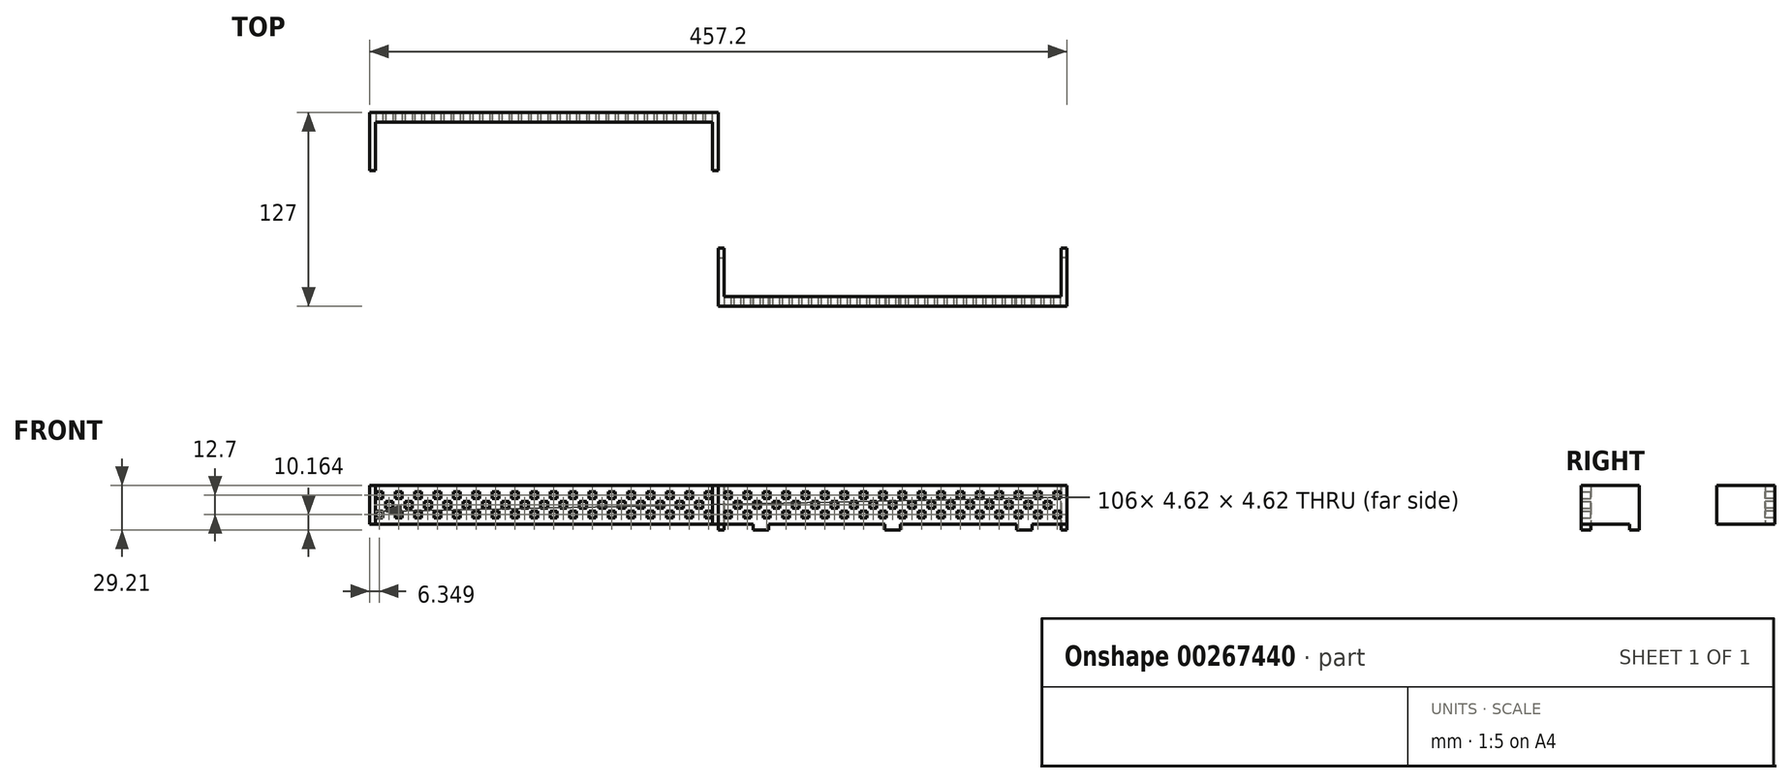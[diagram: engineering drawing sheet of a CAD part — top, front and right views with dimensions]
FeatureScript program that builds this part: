
annotation { "Feature Type Name" : "Feature", "Feature Type Description" : "" }
export const myFeature = defineFeature(function(context is Context, id is Id, definition is map)
    precondition{}
    {
        {
            var Q0;
            Q0=qCreatedBy(makeId("Front.planeOp"),FACE);
            var sketch = newSketch(context, id + "F0", { "sketchPlane" : qUnion([Q0])});
            skLineSegment(sketch, "E0", {"start": v(-96.7, -7.19) * mm, "end": v(-84, -7.19) * mm});
            skLineSegment(sketch, "E1.1.0.0", {"start": v(-84, -7.19) * mm, "end": v(-71.3, -7.19) * mm});
            skLineSegment(sketch, "E1.2.0.0", {"start": v(-71.3, -7.19) * mm, "end": v(-58.6, -7.19) * mm});
            skLineSegment(sketch, "E1.3.0.0", {"start": v(-58.6, -7.19) * mm, "end": v(-45.9, -7.19) * mm});
            skLineSegment(sketch, "E1.4.0.0", {"start": v(-45.9, -7.19) * mm, "end": v(-33.2, -7.19) * mm});
            skLineSegment(sketch, "E1.5.0.0", {"start": v(-33.2, -7.19) * mm, "end": v(-20.5, -7.19) * mm});
            skLineSegment(sketch, "E1.6.0.0", {"start": v(-20.5, -7.19) * mm, "end": v(-7.8, -7.19) * mm});
            skLineSegment(sketch, "E1.7.0.0", {"start": v(-7.8, -7.19) * mm, "end": v(4.9, -7.19) * mm});
            skLineSegment(sketch, "E1.8.0.0", {"start": v(4.9, -7.19) * mm, "end": v(17.6, -7.19) * mm});
            skLineSegment(sketch, "E1.9.0.0", {"start": v(17.6, -7.19) * mm, "end": v(30.3, -7.19) * mm});
            skLineSegment(sketch, "E1.10.0.0", {"start": v(30.3, -7.19) * mm, "end": v(43, -7.19) * mm});
            skLineSegment(sketch, "E1.11.0.0", {"start": v(43, -7.19) * mm, "end": v(55.7, -7.19) * mm});
            skLineSegment(sketch, "E1.12.0.0", {"start": v(55.7, -7.19) * mm, "end": v(68.4, -7.19) * mm});
            skLineSegment(sketch, "E1.13.0.0", {"start": v(68.4, -7.19) * mm, "end": v(81.1, -7.19) * mm});
            skLineSegment(sketch, "E1.14.0.0", {"start": v(81.1, -7.19) * mm, "end": v(93.8, -7.19) * mm});
            skLineSegment(sketch, "E1.direction1", {"start": v(-96.7, -7.19) * mm, "end": v(-84, -7.19) * mm, "construction": true});
            skLineSegment(sketch, "E2", {"start": v(-96.7, -7.19) * mm, "end": v(-96.7, 5.51) * mm});
            skLineSegment(sketch, "E3", {"start": v(-96.7, -0.84) * mm, "end": v(-84.12, -0.84) * mm});
            skPoint(sketch, "E3.endSnap0", {"position": v(-96.7, -0.84) * mm});
            skLineSegment(sketch, "E4.MirrorCS", {"start": v(-96.7, 5.51) * mm, "end": v(-84, 5.51) * mm, "construction": true});
            skLineSegment(sketch, "E5.MirrorCS", {"start": v(-84, 5.51) * mm, "end": v(-71.3, 5.51) * mm});
            skLineSegment(sketch, "E6.MirrorCS", {"start": v(-71.3, 5.51) * mm, "end": v(-58.6, 5.51) * mm});
            skLineSegment(sketch, "E7.MirrorCS", {"start": v(-58.6, 5.51) * mm, "end": v(-45.9, 5.51) * mm});
            skLineSegment(sketch, "E8.MirrorCS", {"start": v(-45.9, 5.51) * mm, "end": v(-33.2, 5.51) * mm});
            skLineSegment(sketch, "E9.MirrorCS", {"start": v(-33.2, 5.51) * mm, "end": v(-20.5, 5.51) * mm});
            skLineSegment(sketch, "E10.MirrorCS", {"start": v(-20.5, 5.51) * mm, "end": v(-7.8, 5.51) * mm});
            skLineSegment(sketch, "E11.MirrorCS", {"start": v(-7.8, 5.51) * mm, "end": v(-5.49, 5.51) * mm});
            skLineSegment(sketch, "E12.MirrorCS", {"start": v(4.9, 5.51) * mm, "end": v(7.21, 5.51) * mm});
            skLineSegment(sketch, "E13.MirrorCS", {"start": v(17.6, 5.51) * mm, "end": v(19.91, 5.51) * mm});
            skLineSegment(sketch, "E14.MirrorCS", {"start": v(55.7, 5.51) * mm, "end": v(68.4, 5.51) * mm});
            skLineSegment(sketch, "E15.MirrorCS", {"start": v(55.7, 5.51) * mm, "end": v(58.01, 5.51) * mm});
            skLineSegment(sketch, "E16.MirrorCS", {"start": v(30.3, 5.51) * mm, "end": v(32.61, 5.51) * mm});
            skLineSegment(sketch, "E17.MirrorCS", {"start": v(68.4, 5.51) * mm, "end": v(81.1, 5.51) * mm});
            skLineSegment(sketch, "E18.MirrorCS", {"start": v(81.1, 5.51) * mm, "end": v(93.8, 5.51) * mm});
            skLineSegment(sketch, "E19.MirrorCS", {"start": v(43, 5.51) * mm, "end": v(45.31, 5.51) * mm});
            skLineSegment(sketch, "E20.bottom", {"start": v(-99.01, -9.5) * mm, "end": v(-94.39, -9.5) * mm});
            skLineSegment(sketch, "E20.top", {"start": v(-99.01, -4.87) * mm, "end": v(-94.39, -4.87) * mm});
            skLineSegment(sketch, "E20.left", {"start": v(-99.01, -9.5) * mm, "end": v(-99.01, -4.87) * mm});
            skLineSegment(sketch, "E20.right", {"start": v(-94.39, -9.5) * mm, "end": v(-94.39, -4.87) * mm});
            skPoint(sketch, "E20.middle", {"position": v(-96.7, -7.19) * mm});
            skLineSegment(sketch, "E21.0.1.0", {"start": v(-94.39, 3.2) * mm, "end": v(-94.39, 7.83) * mm});
            skLineSegment(sketch, "E21.0.1.1", {"start": v(-99.01, 3.2) * mm, "end": v(-99.01, 7.83) * mm});
            skLineSegment(sketch, "E21.0.1.2", {"start": v(-99.01, 7.83) * mm, "end": v(-94.39, 7.83) * mm});
            skLineSegment(sketch, "E21.0.1.3", {"start": v(-99.01, 3.2) * mm, "end": v(-94.39, 3.2) * mm});
            skLineSegment(sketch, "E21.1.0.0", {"start": v(-81.69, -9.5) * mm, "end": v(-81.69, -4.87) * mm});
            skLineSegment(sketch, "E21.1.0.1", {"start": v(-86.31, -9.5) * mm, "end": v(-86.31, -4.87) * mm});
            skLineSegment(sketch, "E21.1.0.2", {"start": v(-86.31, -4.87) * mm, "end": v(-81.69, -4.87) * mm});
            skLineSegment(sketch, "E21.1.0.3", {"start": v(-86.31, -9.5) * mm, "end": v(-81.69, -9.5) * mm});
            skLineSegment(sketch, "E21.1.1.0", {"start": v(-81.69, 3.2) * mm, "end": v(-81.69, 7.83) * mm});
            skLineSegment(sketch, "E21.1.1.1", {"start": v(-86.31, 3.2) * mm, "end": v(-86.31, 7.83) * mm});
            skLineSegment(sketch, "E21.1.1.2", {"start": v(-86.31, 7.83) * mm, "end": v(-81.69, 7.83) * mm});
            skLineSegment(sketch, "E21.1.1.3", {"start": v(-86.31, 3.2) * mm, "end": v(-81.69, 3.2) * mm});
            skLineSegment(sketch, "E21.2.0.0", {"start": v(-68.99, -9.5) * mm, "end": v(-68.99, -4.87) * mm});
            skLineSegment(sketch, "E21.2.0.1", {"start": v(-73.61, -9.5) * mm, "end": v(-73.61, -4.87) * mm});
            skLineSegment(sketch, "E21.2.0.2", {"start": v(-73.61, -4.87) * mm, "end": v(-68.99, -4.87) * mm});
            skLineSegment(sketch, "E21.2.0.3", {"start": v(-73.61, -9.5) * mm, "end": v(-68.99, -9.5) * mm});
            skLineSegment(sketch, "E21.2.1.0", {"start": v(-68.99, 3.2) * mm, "end": v(-68.99, 7.83) * mm});
            skLineSegment(sketch, "E21.2.1.1", {"start": v(-73.61, 3.2) * mm, "end": v(-73.61, 7.83) * mm});
            skLineSegment(sketch, "E21.2.1.2", {"start": v(-73.61, 7.83) * mm, "end": v(-68.99, 7.83) * mm});
            skLineSegment(sketch, "E21.2.1.3", {"start": v(-73.61, 3.2) * mm, "end": v(-68.99, 3.2) * mm});
            skLineSegment(sketch, "E21.3.0.0", {"start": v(-56.29, -9.5) * mm, "end": v(-56.29, -4.87) * mm});
            skLineSegment(sketch, "E21.3.0.1", {"start": v(-60.91, -9.5) * mm, "end": v(-60.91, -4.87) * mm});
            skLineSegment(sketch, "E21.3.0.2", {"start": v(-60.91, -4.87) * mm, "end": v(-56.29, -4.87) * mm});
            skLineSegment(sketch, "E21.3.0.3", {"start": v(-60.91, -9.5) * mm, "end": v(-56.29, -9.5) * mm});
            skLineSegment(sketch, "E21.3.1.0", {"start": v(-56.29, 3.2) * mm, "end": v(-56.29, 7.83) * mm});
            skLineSegment(sketch, "E21.3.1.1", {"start": v(-60.91, 3.2) * mm, "end": v(-60.91, 7.83) * mm});
            skLineSegment(sketch, "E21.3.1.2", {"start": v(-60.91, 7.83) * mm, "end": v(-56.29, 7.83) * mm});
            skLineSegment(sketch, "E21.3.1.3", {"start": v(-60.91, 3.2) * mm, "end": v(-56.29, 3.2) * mm});
            skLineSegment(sketch, "E21.4.0.0", {"start": v(-43.59, -9.5) * mm, "end": v(-43.59, -4.87) * mm});
            skLineSegment(sketch, "E21.4.0.1", {"start": v(-48.21, -9.5) * mm, "end": v(-48.21, -4.87) * mm});
            skLineSegment(sketch, "E21.4.0.2", {"start": v(-48.21, -4.87) * mm, "end": v(-43.59, -4.87) * mm});
            skLineSegment(sketch, "E21.4.0.3", {"start": v(-48.21, -9.5) * mm, "end": v(-43.59, -9.5) * mm});
            skLineSegment(sketch, "E21.4.1.0", {"start": v(-43.59, 3.2) * mm, "end": v(-43.59, 7.83) * mm});
            skLineSegment(sketch, "E21.4.1.1", {"start": v(-48.21, 3.2) * mm, "end": v(-48.21, 7.83) * mm});
            skLineSegment(sketch, "E21.4.1.2", {"start": v(-48.21, 7.83) * mm, "end": v(-43.59, 7.83) * mm});
            skLineSegment(sketch, "E21.4.1.3", {"start": v(-48.21, 3.2) * mm, "end": v(-43.59, 3.2) * mm});
            skLineSegment(sketch, "E21.5.0.0", {"start": v(-30.89, -9.5) * mm, "end": v(-30.89, -4.87) * mm});
            skLineSegment(sketch, "E21.5.0.1", {"start": v(-35.51, -9.5) * mm, "end": v(-35.51, -4.87) * mm});
            skLineSegment(sketch, "E21.5.0.2", {"start": v(-35.51, -4.87) * mm, "end": v(-30.89, -4.87) * mm});
            skLineSegment(sketch, "E21.5.0.3", {"start": v(-35.51, -9.5) * mm, "end": v(-30.89, -9.5) * mm});
            skLineSegment(sketch, "E21.5.1.0", {"start": v(-30.89, 3.2) * mm, "end": v(-30.89, 7.83) * mm});
            skLineSegment(sketch, "E21.5.1.1", {"start": v(-35.51, 3.2) * mm, "end": v(-35.51, 7.83) * mm});
            skLineSegment(sketch, "E21.5.1.2", {"start": v(-35.51, 7.83) * mm, "end": v(-30.89, 7.83) * mm});
            skLineSegment(sketch, "E21.5.1.3", {"start": v(-35.51, 3.2) * mm, "end": v(-30.89, 3.2) * mm});
            skLineSegment(sketch, "E21.6.0.0", {"start": v(-18.19, -9.5) * mm, "end": v(-18.19, -4.87) * mm});
            skLineSegment(sketch, "E21.6.0.1", {"start": v(-22.81, -9.5) * mm, "end": v(-22.81, -4.87) * mm});
            skLineSegment(sketch, "E21.6.0.2", {"start": v(-22.81, -4.87) * mm, "end": v(-18.19, -4.87) * mm});
            skLineSegment(sketch, "E21.6.0.3", {"start": v(-22.81, -9.5) * mm, "end": v(-18.19, -9.5) * mm});
            skLineSegment(sketch, "E21.6.1.0", {"start": v(-18.19, 3.2) * mm, "end": v(-18.19, 7.83) * mm});
            skLineSegment(sketch, "E21.6.1.1", {"start": v(-22.81, 3.2) * mm, "end": v(-22.81, 7.83) * mm});
            skLineSegment(sketch, "E21.6.1.2", {"start": v(-22.81, 7.83) * mm, "end": v(-18.19, 7.83) * mm});
            skLineSegment(sketch, "E21.6.1.3", {"start": v(-22.81, 3.2) * mm, "end": v(-18.19, 3.2) * mm});
            skLineSegment(sketch, "E21.7.0.0", {"start": v(-5.49, -9.5) * mm, "end": v(-5.49, -4.87) * mm});
            skLineSegment(sketch, "E21.7.0.1", {"start": v(-10.11, -9.5) * mm, "end": v(-10.11, -4.87) * mm});
            skLineSegment(sketch, "E21.7.0.2", {"start": v(-10.11, -4.87) * mm, "end": v(-5.49, -4.87) * mm});
            skLineSegment(sketch, "E21.7.0.3", {"start": v(-10.11, -9.5) * mm, "end": v(-5.49, -9.5) * mm});
            skLineSegment(sketch, "E21.7.1.0", {"start": v(-5.49, 3.2) * mm, "end": v(-5.49, 7.83) * mm});
            skLineSegment(sketch, "E21.7.1.1", {"start": v(-10.11, 3.2) * mm, "end": v(-10.11, 7.83) * mm});
            skLineSegment(sketch, "E21.7.1.2", {"start": v(-10.11, 7.83) * mm, "end": v(-5.49, 7.83) * mm});
            skLineSegment(sketch, "E21.7.1.3", {"start": v(-10.11, 3.2) * mm, "end": v(-5.49, 3.2) * mm});
            skLineSegment(sketch, "E21.8.0.0", {"start": v(7.21, -9.5) * mm, "end": v(7.21, -4.87) * mm});
            skLineSegment(sketch, "E21.8.0.1", {"start": v(2.59, -9.5) * mm, "end": v(2.59, -4.87) * mm});
            skLineSegment(sketch, "E21.8.0.2", {"start": v(2.59, -4.87) * mm, "end": v(7.21, -4.87) * mm});
            skLineSegment(sketch, "E21.8.0.3", {"start": v(2.59, -9.5) * mm, "end": v(7.21, -9.5) * mm});
            skLineSegment(sketch, "E21.8.1.0", {"start": v(7.21, 3.2) * mm, "end": v(7.21, 7.83) * mm});
            skLineSegment(sketch, "E21.8.1.1", {"start": v(2.59, 3.2) * mm, "end": v(2.59, 7.83) * mm});
            skLineSegment(sketch, "E21.8.1.2", {"start": v(2.59, 7.83) * mm, "end": v(7.21, 7.83) * mm});
            skLineSegment(sketch, "E21.8.1.3", {"start": v(2.59, 3.2) * mm, "end": v(7.21, 3.2) * mm});
            skLineSegment(sketch, "E21.9.0.0", {"start": v(19.91, -9.5) * mm, "end": v(19.91, -4.87) * mm});
            skLineSegment(sketch, "E21.9.0.1", {"start": v(15.29, -9.5) * mm, "end": v(15.29, -4.87) * mm});
            skLineSegment(sketch, "E21.9.0.2", {"start": v(15.29, -4.87) * mm, "end": v(19.91, -4.87) * mm});
            skLineSegment(sketch, "E21.9.0.3", {"start": v(15.29, -9.5) * mm, "end": v(19.91, -9.5) * mm});
            skLineSegment(sketch, "E21.9.1.0", {"start": v(19.91, 3.2) * mm, "end": v(19.91, 7.83) * mm});
            skLineSegment(sketch, "E21.9.1.1", {"start": v(15.29, 3.2) * mm, "end": v(15.29, 7.83) * mm});
            skLineSegment(sketch, "E21.9.1.2", {"start": v(15.29, 7.83) * mm, "end": v(19.91, 7.83) * mm});
            skLineSegment(sketch, "E21.9.1.3", {"start": v(15.29, 3.2) * mm, "end": v(19.91, 3.2) * mm});
            skLineSegment(sketch, "E21.10.0.0", {"start": v(32.61, -9.5) * mm, "end": v(32.61, -4.87) * mm});
            skLineSegment(sketch, "E21.10.0.1", {"start": v(27.99, -9.5) * mm, "end": v(27.99, -4.87) * mm});
            skLineSegment(sketch, "E21.10.0.2", {"start": v(27.99, -4.87) * mm, "end": v(32.61, -4.87) * mm});
            skLineSegment(sketch, "E21.10.0.3", {"start": v(27.99, -9.5) * mm, "end": v(32.61, -9.5) * mm});
            skLineSegment(sketch, "E21.10.1.0", {"start": v(32.61, 3.2) * mm, "end": v(32.61, 7.83) * mm});
            skLineSegment(sketch, "E21.10.1.1", {"start": v(27.99, 3.2) * mm, "end": v(27.99, 7.83) * mm});
            skLineSegment(sketch, "E21.10.1.2", {"start": v(27.99, 7.83) * mm, "end": v(32.61, 7.83) * mm});
            skLineSegment(sketch, "E21.10.1.3", {"start": v(27.99, 3.2) * mm, "end": v(32.61, 3.2) * mm});
            skLineSegment(sketch, "E21.11.0.0", {"start": v(45.31, -9.5) * mm, "end": v(45.31, -4.87) * mm});
            skLineSegment(sketch, "E21.11.0.1", {"start": v(40.69, -9.5) * mm, "end": v(40.69, -4.87) * mm});
            skLineSegment(sketch, "E21.11.0.2", {"start": v(40.69, -4.87) * mm, "end": v(45.31, -4.87) * mm});
            skLineSegment(sketch, "E21.11.0.3", {"start": v(40.69, -9.5) * mm, "end": v(45.31, -9.5) * mm});
            skLineSegment(sketch, "E21.11.1.0", {"start": v(45.31, 3.2) * mm, "end": v(45.31, 7.83) * mm});
            skLineSegment(sketch, "E21.11.1.1", {"start": v(40.69, 3.2) * mm, "end": v(40.69, 7.83) * mm});
            skLineSegment(sketch, "E21.11.1.2", {"start": v(40.69, 7.83) * mm, "end": v(45.31, 7.83) * mm});
            skLineSegment(sketch, "E21.11.1.3", {"start": v(40.69, 3.2) * mm, "end": v(45.31, 3.2) * mm});
            skLineSegment(sketch, "E21.12.0.0", {"start": v(58.01, -9.5) * mm, "end": v(58.01, -4.87) * mm});
            skLineSegment(sketch, "E21.12.0.1", {"start": v(53.39, -9.5) * mm, "end": v(53.39, -4.87) * mm});
            skLineSegment(sketch, "E21.12.0.2", {"start": v(53.39, -4.87) * mm, "end": v(58.01, -4.87) * mm});
            skLineSegment(sketch, "E21.12.0.3", {"start": v(53.39, -9.5) * mm, "end": v(58.01, -9.5) * mm});
            skLineSegment(sketch, "E21.12.1.0", {"start": v(58.01, 3.2) * mm, "end": v(58.01, 7.83) * mm});
            skLineSegment(sketch, "E21.12.1.1", {"start": v(53.39, 3.2) * mm, "end": v(53.39, 7.83) * mm});
            skLineSegment(sketch, "E21.12.1.2", {"start": v(53.39, 7.83) * mm, "end": v(58.01, 7.83) * mm});
            skLineSegment(sketch, "E21.12.1.3", {"start": v(53.39, 3.2) * mm, "end": v(58.01, 3.2) * mm});
            skLineSegment(sketch, "E21.13.0.0", {"start": v(70.71, -9.5) * mm, "end": v(70.71, -4.87) * mm});
            skLineSegment(sketch, "E21.13.0.1", {"start": v(66.09, -9.5) * mm, "end": v(66.09, -4.87) * mm});
            skLineSegment(sketch, "E21.13.0.2", {"start": v(66.09, -4.87) * mm, "end": v(70.71, -4.87) * mm});
            skLineSegment(sketch, "E21.13.0.3", {"start": v(66.09, -9.5) * mm, "end": v(70.71, -9.5) * mm});
            skLineSegment(sketch, "E21.13.1.0", {"start": v(70.71, 3.2) * mm, "end": v(70.71, 7.83) * mm});
            skLineSegment(sketch, "E21.13.1.1", {"start": v(66.09, 3.2) * mm, "end": v(66.09, 7.83) * mm});
            skLineSegment(sketch, "E21.13.1.2", {"start": v(66.09, 7.83) * mm, "end": v(70.71, 7.83) * mm});
            skLineSegment(sketch, "E21.13.1.3", {"start": v(66.09, 3.2) * mm, "end": v(70.71, 3.2) * mm});
            skLineSegment(sketch, "E21.14.0.0", {"start": v(83.41, -9.5) * mm, "end": v(83.41, -4.87) * mm});
            skLineSegment(sketch, "E21.14.0.1", {"start": v(78.79, -9.5) * mm, "end": v(78.79, -4.87) * mm});
            skLineSegment(sketch, "E21.14.0.2", {"start": v(78.79, -4.87) * mm, "end": v(83.41, -4.87) * mm});
            skLineSegment(sketch, "E21.14.0.3", {"start": v(78.79, -9.5) * mm, "end": v(83.41, -9.5) * mm});
            skLineSegment(sketch, "E21.14.1.0", {"start": v(83.41, 3.2) * mm, "end": v(83.41, 7.83) * mm});
            skLineSegment(sketch, "E21.14.1.1", {"start": v(78.79, 3.2) * mm, "end": v(78.79, 7.83) * mm});
            skLineSegment(sketch, "E21.14.1.2", {"start": v(78.79, 7.83) * mm, "end": v(83.41, 7.83) * mm});
            skLineSegment(sketch, "E21.14.1.3", {"start": v(78.79, 3.2) * mm, "end": v(83.41, 3.2) * mm});
            skLineSegment(sketch, "E21.direction1", {"start": v(-94.39, -9.5) * mm, "end": v(-81.69, -9.5) * mm, "construction": true});
            skLineSegment(sketch, "E21.direction2", {"start": v(-94.39, -9.5) * mm, "end": v(-94.39, 3.2) * mm, "construction": true});
            skLineSegment(sketch, "E22.bottom", {"start": v(-88.1, -3.15) * mm, "end": v(-92.72, -3.15) * mm});
            skLineSegment(sketch, "E22.top", {"start": v(-88.1, 1.48) * mm, "end": v(-92.72, 1.48) * mm});
            skLineSegment(sketch, "E22.left", {"start": v(-88.1, -3.15) * mm, "end": v(-88.1, 1.48) * mm});
            skLineSegment(sketch, "E22.right", {"start": v(-92.72, -3.15) * mm, "end": v(-92.72, 1.48) * mm});
            skPoint(sketch, "E22.middle", {"position": v(-90.41, -0.84) * mm});
            skLineSegment(sketch, "E23.1.0.0", {"start": v(-75.4, -3.15) * mm, "end": v(-75.4, 1.48) * mm});
            skLineSegment(sketch, "E23.1.0.1", {"start": v(-75.4, 1.48) * mm, "end": v(-80.02, 1.48) * mm});
            skLineSegment(sketch, "E23.1.0.2", {"start": v(-80.02, -3.15) * mm, "end": v(-80.02, 1.48) * mm});
            skLineSegment(sketch, "E23.1.0.3", {"start": v(-75.4, -3.15) * mm, "end": v(-80.02, -3.15) * mm});
            skLineSegment(sketch, "E23.2.0.0", {"start": v(-62.7, -3.15) * mm, "end": v(-62.7, 1.48) * mm});
            skLineSegment(sketch, "E23.2.0.1", {"start": v(-62.7, 1.48) * mm, "end": v(-67.32, 1.48) * mm});
            skLineSegment(sketch, "E23.2.0.2", {"start": v(-67.32, -3.15) * mm, "end": v(-67.32, 1.48) * mm});
            skLineSegment(sketch, "E23.2.0.3", {"start": v(-62.7, -3.15) * mm, "end": v(-67.32, -3.15) * mm});
            skLineSegment(sketch, "E23.3.0.0", {"start": v(-50, -3.15) * mm, "end": v(-50, 1.48) * mm});
            skLineSegment(sketch, "E23.3.0.1", {"start": v(-50, 1.48) * mm, "end": v(-54.62, 1.48) * mm});
            skLineSegment(sketch, "E23.3.0.2", {"start": v(-54.62, -3.15) * mm, "end": v(-54.62, 1.48) * mm});
            skLineSegment(sketch, "E23.3.0.3", {"start": v(-50, -3.15) * mm, "end": v(-54.62, -3.15) * mm});
            skLineSegment(sketch, "E23.4.0.0", {"start": v(-37.3, -3.15) * mm, "end": v(-37.3, 1.48) * mm});
            skLineSegment(sketch, "E23.4.0.1", {"start": v(-37.3, 1.48) * mm, "end": v(-41.92, 1.48) * mm});
            skLineSegment(sketch, "E23.4.0.2", {"start": v(-41.92, -3.15) * mm, "end": v(-41.92, 1.48) * mm});
            skLineSegment(sketch, "E23.4.0.3", {"start": v(-37.3, -3.15) * mm, "end": v(-41.92, -3.15) * mm});
            skLineSegment(sketch, "E23.5.0.0", {"start": v(-24.6, -3.15) * mm, "end": v(-24.6, 1.48) * mm});
            skLineSegment(sketch, "E23.5.0.1", {"start": v(-24.6, 1.48) * mm, "end": v(-29.22, 1.48) * mm});
            skLineSegment(sketch, "E23.5.0.2", {"start": v(-29.22, -3.15) * mm, "end": v(-29.22, 1.48) * mm});
            skLineSegment(sketch, "E23.5.0.3", {"start": v(-24.6, -3.15) * mm, "end": v(-29.22, -3.15) * mm});
            skLineSegment(sketch, "E23.6.0.0", {"start": v(-11.9, -3.15) * mm, "end": v(-11.9, 1.48) * mm});
            skLineSegment(sketch, "E23.6.0.1", {"start": v(-11.9, 1.48) * mm, "end": v(-16.52, 1.48) * mm});
            skLineSegment(sketch, "E23.6.0.2", {"start": v(-16.52, -3.15) * mm, "end": v(-16.52, 1.48) * mm});
            skLineSegment(sketch, "E23.6.0.3", {"start": v(-11.9, -3.15) * mm, "end": v(-16.52, -3.15) * mm});
            skLineSegment(sketch, "E23.7.0.0", {"start": v(0.8, -3.15) * mm, "end": v(0.8, 1.48) * mm});
            skLineSegment(sketch, "E23.7.0.1", {"start": v(0.8, 1.48) * mm, "end": v(-3.82, 1.48) * mm});
            skLineSegment(sketch, "E23.7.0.2", {"start": v(-3.82, -3.15) * mm, "end": v(-3.82, 1.48) * mm});
            skLineSegment(sketch, "E23.7.0.3", {"start": v(0.8, -3.15) * mm, "end": v(-3.82, -3.15) * mm});
            skLineSegment(sketch, "E23.8.0.0", {"start": v(13.5, -3.15) * mm, "end": v(13.5, 1.48) * mm});
            skLineSegment(sketch, "E23.8.0.1", {"start": v(13.5, 1.48) * mm, "end": v(8.88, 1.48) * mm});
            skLineSegment(sketch, "E23.8.0.2", {"start": v(8.88, -3.15) * mm, "end": v(8.88, 1.48) * mm});
            skLineSegment(sketch, "E23.8.0.3", {"start": v(13.5, -3.15) * mm, "end": v(8.88, -3.15) * mm});
            skLineSegment(sketch, "E23.9.0.0", {"start": v(26.2, -3.15) * mm, "end": v(26.2, 1.48) * mm});
            skLineSegment(sketch, "E23.9.0.1", {"start": v(26.2, 1.48) * mm, "end": v(21.58, 1.48) * mm});
            skLineSegment(sketch, "E23.9.0.2", {"start": v(21.58, -3.15) * mm, "end": v(21.58, 1.48) * mm});
            skLineSegment(sketch, "E23.9.0.3", {"start": v(26.2, -3.15) * mm, "end": v(21.58, -3.15) * mm});
            skLineSegment(sketch, "E23.10.0.0", {"start": v(38.9, -3.15) * mm, "end": v(38.9, 1.48) * mm});
            skLineSegment(sketch, "E23.10.0.1", {"start": v(38.9, 1.48) * mm, "end": v(34.28, 1.48) * mm});
            skLineSegment(sketch, "E23.10.0.2", {"start": v(34.28, -3.15) * mm, "end": v(34.28, 1.48) * mm});
            skLineSegment(sketch, "E23.10.0.3", {"start": v(38.9, -3.15) * mm, "end": v(34.28, -3.15) * mm});
            skLineSegment(sketch, "E23.11.0.0", {"start": v(51.6, -3.15) * mm, "end": v(51.6, 1.48) * mm});
            skLineSegment(sketch, "E23.11.0.1", {"start": v(51.6, 1.48) * mm, "end": v(46.98, 1.48) * mm});
            skLineSegment(sketch, "E23.11.0.2", {"start": v(46.98, -3.15) * mm, "end": v(46.98, 1.48) * mm});
            skLineSegment(sketch, "E23.11.0.3", {"start": v(51.6, -3.15) * mm, "end": v(46.98, -3.15) * mm});
            skLineSegment(sketch, "E23.12.0.0", {"start": v(64.3, -3.15) * mm, "end": v(64.3, 1.48) * mm});
            skLineSegment(sketch, "E23.12.0.1", {"start": v(64.3, 1.48) * mm, "end": v(59.68, 1.48) * mm});
            skLineSegment(sketch, "E23.12.0.2", {"start": v(59.68, -3.15) * mm, "end": v(59.68, 1.48) * mm});
            skLineSegment(sketch, "E23.12.0.3", {"start": v(64.3, -3.15) * mm, "end": v(59.68, -3.15) * mm});
            skLineSegment(sketch, "E23.13.0.0", {"start": v(77, -3.15) * mm, "end": v(77, 1.48) * mm});
            skLineSegment(sketch, "E23.13.0.1", {"start": v(77, 1.48) * mm, "end": v(72.38, 1.48) * mm});
            skLineSegment(sketch, "E23.13.0.2", {"start": v(72.38, -3.15) * mm, "end": v(72.38, 1.48) * mm});
            skLineSegment(sketch, "E23.13.0.3", {"start": v(77, -3.15) * mm, "end": v(72.38, -3.15) * mm});
            skLineSegment(sketch, "E23.direction1", {"start": v(-88.1, -3.15) * mm, "end": v(-75.4, -3.15) * mm, "construction": true});
            skLineSegment(sketch, "E24.top", {"start": v(-99.01, -13.54) * mm, "end": v(-103.05, -13.54) * mm});
            skLineSegment(sketch, "E24.right", {"start": v(-103.05, -9.5) * mm, "end": v(-103.05, -13.54) * mm});
            skLineSegment(sketch, "E25.1.0.0", {"start": v(96.11, 3.2) * mm, "end": v(96.11, 7.83) * mm});
            skLineSegment(sketch, "E25.1.0.1", {"start": v(91.49, 7.83) * mm, "end": v(96.11, 7.83) * mm});
            skLineSegment(sketch, "E25.1.0.2", {"start": v(91.49, 3.2) * mm, "end": v(91.49, 7.83) * mm});
            skLineSegment(sketch, "E25.1.0.3", {"start": v(91.49, 3.2) * mm, "end": v(96.11, 3.2) * mm});
            skLineSegment(sketch, "E25.1.0.4", {"start": v(89.7, -3.15) * mm, "end": v(89.7, 1.48) * mm});
            skLineSegment(sketch, "E25.1.0.5", {"start": v(89.7, 1.48) * mm, "end": v(85.08, 1.48) * mm});
            skLineSegment(sketch, "E25.1.0.6", {"start": v(85.08, -3.15) * mm, "end": v(85.08, 1.48) * mm});
            skLineSegment(sketch, "E25.1.0.7", {"start": v(89.7, -3.15) * mm, "end": v(85.08, -3.15) * mm});
            skLineSegment(sketch, "E25.1.0.8", {"start": v(91.49, -4.87) * mm, "end": v(96.11, -4.87) * mm});
            skLineSegment(sketch, "E25.1.0.9", {"start": v(91.49, -9.5) * mm, "end": v(91.49, -4.87) * mm});
            skLineSegment(sketch, "E25.1.0.10", {"start": v(91.49, -9.5) * mm, "end": v(96.11, -9.5) * mm});
            skLineSegment(sketch, "E25.1.0.11", {"start": v(96.11, -9.5) * mm, "end": v(96.11, -4.87) * mm});
            skLineSegment(sketch, "E25.2.0.0", {"start": v(108.81, 3.2) * mm, "end": v(108.81, 7.83) * mm});
            skLineSegment(sketch, "E25.2.0.1", {"start": v(104.19, 7.83) * mm, "end": v(108.81, 7.83) * mm});
            skLineSegment(sketch, "E25.2.0.2", {"start": v(104.19, 3.2) * mm, "end": v(104.19, 7.83) * mm});
            skLineSegment(sketch, "E25.2.0.3", {"start": v(104.19, 3.2) * mm, "end": v(108.81, 3.2) * mm});
            skLineSegment(sketch, "E25.2.0.4", {"start": v(102.4, -3.15) * mm, "end": v(102.4, 1.48) * mm});
            skLineSegment(sketch, "E25.2.0.5", {"start": v(102.4, 1.48) * mm, "end": v(97.78, 1.48) * mm});
            skLineSegment(sketch, "E25.2.0.6", {"start": v(97.78, -3.15) * mm, "end": v(97.78, 1.48) * mm});
            skLineSegment(sketch, "E25.2.0.7", {"start": v(102.4, -3.15) * mm, "end": v(97.78, -3.15) * mm});
            skLineSegment(sketch, "E25.2.0.8", {"start": v(104.19, -4.87) * mm, "end": v(108.81, -4.87) * mm});
            skLineSegment(sketch, "E25.2.0.9", {"start": v(104.19, -9.5) * mm, "end": v(104.19, -4.87) * mm});
            skLineSegment(sketch, "E25.2.0.10", {"start": v(104.19, -9.5) * mm, "end": v(108.81, -9.5) * mm});
            skLineSegment(sketch, "E25.2.0.11", {"start": v(108.81, -9.5) * mm, "end": v(108.81, -4.87) * mm});
            skLineSegment(sketch, "E25.direction1", {"start": v(78.79, -9.5) * mm, "end": v(91.49, -9.5) * mm, "construction": true});
            skLineSegment(sketch, "E26.1.0.0", {"start": v(115.1, -3.15) * mm, "end": v(115.1, 1.48) * mm});
            skLineSegment(sketch, "E26.1.0.1", {"start": v(115.1, 1.48) * mm, "end": v(110.48, 1.48) * mm});
            skLineSegment(sketch, "E26.1.0.2", {"start": v(110.48, -3.15) * mm, "end": v(110.48, 1.48) * mm});
            skLineSegment(sketch, "E26.1.0.3", {"start": v(115.1, -3.15) * mm, "end": v(110.48, -3.15) * mm});
            skLineSegment(sketch, "E26.1.0.4", {"start": v(116.89, -9.5) * mm, "end": v(116.89, -4.87) * mm});
            skLineSegment(sketch, "E26.1.0.5", {"start": v(116.89, -9.5) * mm, "end": v(121.51, -9.5) * mm});
            skLineSegment(sketch, "E26.1.0.6", {"start": v(121.51, -9.5) * mm, "end": v(121.51, -4.87) * mm});
            skLineSegment(sketch, "E26.1.0.7", {"start": v(116.89, -4.87) * mm, "end": v(121.51, -4.87) * mm});
            skLineSegment(sketch, "E26.1.0.8", {"start": v(116.89, 3.2) * mm, "end": v(121.51, 3.2) * mm});
            skLineSegment(sketch, "E26.1.0.9", {"start": v(116.89, 3.2) * mm, "end": v(116.89, 7.83) * mm});
            skLineSegment(sketch, "E26.1.0.10", {"start": v(116.89, 7.83) * mm, "end": v(121.51, 7.83) * mm});
            skLineSegment(sketch, "E26.1.0.11", {"start": v(121.51, 3.2) * mm, "end": v(121.51, 7.83) * mm});
            skLineSegment(sketch, "E26.direction1", {"start": v(104.19, -9.5) * mm, "end": v(116.89, -9.5) * mm, "construction": true});
            skLineSegment(sketch, "E27.top", {"start": v(121.51, 11.86) * mm, "end": v(125.55, 11.86) * mm});
            skLineSegment(sketch, "E27.right", {"start": v(125.55, 7.83) * mm, "end": v(125.55, 11.86) * mm});
            skLineSegment(sketch, "E28.bottom", {"start": v(125.55, 11.86) * mm, "end": v(-103.05, 11.86) * mm});
            skLineSegment(sketch, "E28.top", {"start": v(125.55, -13.54) * mm, "end": v(-103.05, -13.54) * mm});
            skLineSegment(sketch, "E28.left", {"start": v(125.55, 11.86) * mm, "end": v(125.55, -13.54) * mm});
            skLineSegment(sketch, "E28.right", {"start": v(-103.05, 11.86) * mm, "end": v(-103.05, -13.54) * mm});
            skLineSegment(sketch, "E29.trimOffspring", {"start": v(2.59, 5.51) * mm, "end": v(4.9, 5.51) * mm});
            skLineSegment(sketch, "E30.trimOffspring", {"start": v(15.29, 5.51) * mm, "end": v(17.6, 5.51) * mm});
            skLineSegment(sketch, "E31.trimOffspring", {"start": v(27.99, 5.51) * mm, "end": v(30.3, 5.51) * mm});
            skLineSegment(sketch, "E32.trimOffspring", {"start": v(40.69, 5.51) * mm, "end": v(43, 5.51) * mm});
            skLineSegment(sketch, "E33.trimOffspring", {"start": v(53.39, 5.51) * mm, "end": v(55.7, 5.51) * mm});
            skLineSegment(sketch, "E34.trimOffspring", {"start": v(66.09, 5.51) * mm, "end": v(68.4, 5.51) * mm});
            skSolve(sketch);
        }
        {
            var Q0;
            {var subQ113=sQuery(id+"F0.wireOp",EDGE,"E20.bottom");Q0=makeQuery(id+"F0.imprint","IMPRINT",FACE,{"disambiguationData":[TD([[makeQuery(id+"F0.imprint","IMPRINT",EDGE,{"derivedFrom":subQ113}),-1.0]])]});}
            extrude(context, id + "F1", {"entities" : qUnion([Q0]), "depth" : 6.35 * mm});
        }
        {
            var Q0;
            Q0=makeQuery(id+"F1.opExtrude","SWEPT_FACE",FACE,{"disambiguationData":[OSD([sQuery(id+"F0.wireOp",EDGE,"E28.right")])]});
            var sketch = newSketch(context, id + "F2", { "sketchPlane" : qUnion([Q0])});
            skLineSegment(sketch, "E35", {"start": v(6.35, 11.86) * mm, "end": v(-31.75, 11.86) * mm});
            skLineSegment(sketch, "E36", {"start": v(6.35, -13.54) * mm, "end": v(-31.75, -13.54) * mm});
            skLineSegment(sketch, "E37", {"start": v(-31.75, -13.54) * mm, "end": v(-31.75, 11.86) * mm});
            skLineSegment(sketch, "E38", {"start": v(0, 11.86) * mm, "end": v(0, -13.54) * mm});
            skSolve(sketch);
        }
        {
            var Q0;
            {var subQ2=sQuery(id+"F2.wireOp",EDGE,"E37");Q0=makeQuery(id+"F2.imprint","IMPRINT",FACE,{"disambiguationData":[TD([[makeQuery(id+"F2.imprint","IMPRINT",EDGE,{"derivedFrom":subQ2}),-1.0]])]});}
            extrude(context, id + "F3", {"entities" : qUnion([Q0]), "operationType" : NewBodyOperationType.ADD, "oppositeDirection" : true, "depth" : 3.8 * mm});
        }
        {
            var Q0;
            Q0=makeQuery(id+"F1.opExtrude","SWEPT_FACE",FACE,{"disambiguationData":[OSD([sQuery(id+"F0.wireOp",EDGE,"E28.left")])]});
            var sketch = newSketch(context, id + "F4", { "sketchPlane" : qUnion([Q0])});
            skLineSegment(sketch, "E39", {"start": v(-6.35, 11.86) * mm, "end": v(31.75, 11.86) * mm});
            skPoint(sketch, "E39.endSnap0", {"position": v(-3.18, 11.86) * mm});
            skLineSegment(sketch, "E40", {"start": v(-6.35, -13.54) * mm, "end": v(31.75, -13.54) * mm});
            skLineSegment(sketch, "E41", {"start": v(31.75, -13.54) * mm, "end": v(31.75, 11.86) * mm});
            skLineSegment(sketch, "E42", {"start": v(0, 11.86) * mm, "end": v(0, -13.54) * mm});
            skSolve(sketch);
        }
        {
            var Q0;
            {var subQ2=sQuery(id+"F4.wireOp",EDGE,"E41");Q0=makeQuery(id+"F4.imprint","IMPRINT",FACE,{"disambiguationData":[TD([[makeQuery(id+"F4.imprint","IMPRINT",EDGE,{"derivedFrom":subQ2}),1.0]])]});}
            extrude(context, id + "F5", {"entities" : qUnion([Q0]), "operationType" : NewBodyOperationType.ADD, "oppositeDirection" : true, "depth" : 3.8 * mm});
        }
        {
            var Q0;
            Q0=makeQuery(id+"F1.opExtrude","SWEPT_BODY",BODY,{"disambiguationData":[OSD([sQuery(id+"F0.wireOp",EDGE,"E20.bottom"),sQuery(id+"F0.wireOp",EDGE,"E20.top"),sQuery(id+"F0.wireOp",EDGE,"E20.left"),sQuery(id+"F0.wireOp",EDGE,"E20.right"),sQuery(id+"F0.wireOp",EDGE,"E21.0.1.0"),sQuery(id+"F0.wireOp",EDGE,"E21.0.1.1"),sQuery(id+"F0.wireOp",EDGE,"E21.0.1.2"),sQuery(id+"F0.wireOp",EDGE,"E21.0.1.3"),sQuery(id+"F0.wireOp",EDGE,"E21.1.0.0"),sQuery(id+"F0.wireOp",EDGE,"E21.1.0.1"),sQuery(id+"F0.wireOp",EDGE,"E21.1.0.2"),sQuery(id+"F0.wireOp",EDGE,"E21.1.0.3"),sQuery(id+"F0.wireOp",EDGE,"E21.1.1.0"),sQuery(id+"F0.wireOp",EDGE,"E21.1.1.1"),sQuery(id+"F0.wireOp",EDGE,"E21.1.1.2"),sQuery(id+"F0.wireOp",EDGE,"E21.1.1.3"),sQuery(id+"F0.wireOp",EDGE,"E21.2.0.0"),sQuery(id+"F0.wireOp",EDGE,"E21.2.0.1"),sQuery(id+"F0.wireOp",EDGE,"E21.2.0.2"),sQuery(id+"F0.wireOp",EDGE,"E21.2.0.3"),sQuery(id+"F0.wireOp",EDGE,"E21.2.1.0"),sQuery(id+"F0.wireOp",EDGE,"E21.2.1.1"),sQuery(id+"F0.wireOp",EDGE,"E21.2.1.2"),sQuery(id+"F0.wireOp",EDGE,"E21.2.1.3"),sQuery(id+"F0.wireOp",EDGE,"E21.3.0.0"),sQuery(id+"F0.wireOp",EDGE,"E21.3.0.1"),sQuery(id+"F0.wireOp",EDGE,"E21.3.0.2"),sQuery(id+"F0.wireOp",EDGE,"E21.3.0.3"),sQuery(id+"F0.wireOp",EDGE,"E21.3.1.0"),sQuery(id+"F0.wireOp",EDGE,"E21.3.1.1"),sQuery(id+"F0.wireOp",EDGE,"E21.3.1.2"),sQuery(id+"F0.wireOp",EDGE,"E21.3.1.3"),sQuery(id+"F0.wireOp",EDGE,"E21.4.0.0"),sQuery(id+"F0.wireOp",EDGE,"E21.4.0.1"),sQuery(id+"F0.wireOp",EDGE,"E21.4.0.2"),sQuery(id+"F0.wireOp",EDGE,"E21.4.0.3"),sQuery(id+"F0.wireOp",EDGE,"E21.4.1.0"),sQuery(id+"F0.wireOp",EDGE,"E21.4.1.1"),sQuery(id+"F0.wireOp",EDGE,"E21.4.1.2"),sQuery(id+"F0.wireOp",EDGE,"E21.4.1.3"),sQuery(id+"F0.wireOp",EDGE,"E21.5.0.0"),sQuery(id+"F0.wireOp",EDGE,"E21.5.0.1"),sQuery(id+"F0.wireOp",EDGE,"E21.5.0.2"),sQuery(id+"F0.wireOp",EDGE,"E21.5.0.3"),sQuery(id+"F0.wireOp",EDGE,"E21.5.1.0"),sQuery(id+"F0.wireOp",EDGE,"E21.5.1.1"),sQuery(id+"F0.wireOp",EDGE,"E21.5.1.2"),sQuery(id+"F0.wireOp",EDGE,"E21.5.1.3"),sQuery(id+"F0.wireOp",EDGE,"E21.6.0.0"),sQuery(id+"F0.wireOp",EDGE,"E21.6.0.1"),sQuery(id+"F0.wireOp",EDGE,"E21.6.0.2"),sQuery(id+"F0.wireOp",EDGE,"E21.6.0.3"),sQuery(id+"F0.wireOp",EDGE,"E21.6.1.0"),sQuery(id+"F0.wireOp",EDGE,"E21.6.1.1"),sQuery(id+"F0.wireOp",EDGE,"E21.6.1.2"),sQuery(id+"F0.wireOp",EDGE,"E21.6.1.3"),sQuery(id+"F0.wireOp",EDGE,"E21.7.0.0"),sQuery(id+"F0.wireOp",EDGE,"E21.7.0.1"),sQuery(id+"F0.wireOp",EDGE,"E21.7.0.2"),sQuery(id+"F0.wireOp",EDGE,"E21.7.0.3"),sQuery(id+"F0.wireOp",EDGE,"E21.7.1.0"),sQuery(id+"F0.wireOp",EDGE,"E21.7.1.1"),sQuery(id+"F0.wireOp",EDGE,"E21.7.1.2"),sQuery(id+"F0.wireOp",EDGE,"E21.7.1.3"),sQuery(id+"F0.wireOp",EDGE,"E21.8.0.0"),sQuery(id+"F0.wireOp",EDGE,"E21.8.0.1"),sQuery(id+"F0.wireOp",EDGE,"E21.8.0.2"),sQuery(id+"F0.wireOp",EDGE,"E21.8.0.3"),sQuery(id+"F0.wireOp",EDGE,"E21.8.1.0"),sQuery(id+"F0.wireOp",EDGE,"E21.8.1.1"),sQuery(id+"F0.wireOp",EDGE,"E21.8.1.2"),sQuery(id+"F0.wireOp",EDGE,"E21.8.1.3"),sQuery(id+"F0.wireOp",EDGE,"E21.9.0.0"),sQuery(id+"F0.wireOp",EDGE,"E21.9.0.1"),sQuery(id+"F0.wireOp",EDGE,"E21.9.0.2"),sQuery(id+"F0.wireOp",EDGE,"E21.9.0.3"),sQuery(id+"F0.wireOp",EDGE,"E21.9.1.0"),sQuery(id+"F0.wireOp",EDGE,"E21.9.1.1"),sQuery(id+"F0.wireOp",EDGE,"E21.9.1.2"),sQuery(id+"F0.wireOp",EDGE,"E21.9.1.3"),sQuery(id+"F0.wireOp",EDGE,"E21.10.0.0"),sQuery(id+"F0.wireOp",EDGE,"E21.10.0.1"),sQuery(id+"F0.wireOp",EDGE,"E21.10.0.2"),sQuery(id+"F0.wireOp",EDGE,"E21.10.0.3"),sQuery(id+"F0.wireOp",EDGE,"E21.10.1.0"),sQuery(id+"F0.wireOp",EDGE,"E21.10.1.1"),sQuery(id+"F0.wireOp",EDGE,"E21.10.1.2"),sQuery(id+"F0.wireOp",EDGE,"E21.10.1.3"),sQuery(id+"F0.wireOp",EDGE,"E21.11.0.0"),sQuery(id+"F0.wireOp",EDGE,"E21.11.0.1"),sQuery(id+"F0.wireOp",EDGE,"E21.11.0.2"),sQuery(id+"F0.wireOp",EDGE,"E21.11.0.3"),sQuery(id+"F0.wireOp",EDGE,"E21.11.1.0"),sQuery(id+"F0.wireOp",EDGE,"E21.11.1.1"),sQuery(id+"F0.wireOp",EDGE,"E21.11.1.2"),sQuery(id+"F0.wireOp",EDGE,"E21.11.1.3"),sQuery(id+"F0.wireOp",EDGE,"E21.12.0.0"),sQuery(id+"F0.wireOp",EDGE,"E21.12.0.1"),sQuery(id+"F0.wireOp",EDGE,"E21.12.0.2"),sQuery(id+"F0.wireOp",EDGE,"E21.12.0.3"),sQuery(id+"F0.wireOp",EDGE,"E21.12.1.0"),sQuery(id+"F0.wireOp",EDGE,"E21.12.1.1"),sQuery(id+"F0.wireOp",EDGE,"E21.12.1.2"),sQuery(id+"F0.wireOp",EDGE,"E21.12.1.3"),sQuery(id+"F0.wireOp",EDGE,"E21.13.0.0"),sQuery(id+"F0.wireOp",EDGE,"E21.13.0.1"),sQuery(id+"F0.wireOp",EDGE,"E21.13.0.2"),sQuery(id+"F0.wireOp",EDGE,"E21.13.0.3"),sQuery(id+"F0.wireOp",EDGE,"E21.13.1.0"),sQuery(id+"F0.wireOp",EDGE,"E21.13.1.1"),sQuery(id+"F0.wireOp",EDGE,"E21.13.1.2"),sQuery(id+"F0.wireOp",EDGE,"E21.13.1.3"),sQuery(id+"F0.wireOp",EDGE,"E21.14.0.0"),sQuery(id+"F0.wireOp",EDGE,"E21.14.0.1"),sQuery(id+"F0.wireOp",EDGE,"E21.14.0.2"),sQuery(id+"F0.wireOp",EDGE,"E21.14.0.3"),sQuery(id+"F0.wireOp",EDGE,"E21.14.1.0"),sQuery(id+"F0.wireOp",EDGE,"E21.14.1.1"),sQuery(id+"F0.wireOp",EDGE,"E21.14.1.2"),sQuery(id+"F0.wireOp",EDGE,"E21.14.1.3"),sQuery(id+"F0.wireOp",EDGE,"E22.bottom"),sQuery(id+"F0.wireOp",EDGE,"E22.top"),sQuery(id+"F0.wireOp",EDGE,"E22.left"),sQuery(id+"F0.wireOp",EDGE,"E22.right"),sQuery(id+"F0.wireOp",EDGE,"E23.1.0.0"),sQuery(id+"F0.wireOp",EDGE,"E23.1.0.1"),sQuery(id+"F0.wireOp",EDGE,"E23.1.0.2"),sQuery(id+"F0.wireOp",EDGE,"E23.1.0.3"),sQuery(id+"F0.wireOp",EDGE,"E23.2.0.0"),sQuery(id+"F0.wireOp",EDGE,"E23.2.0.1"),sQuery(id+"F0.wireOp",EDGE,"E23.2.0.2"),sQuery(id+"F0.wireOp",EDGE,"E23.2.0.3"),sQuery(id+"F0.wireOp",EDGE,"E23.3.0.0"),sQuery(id+"F0.wireOp",EDGE,"E23.3.0.1"),sQuery(id+"F0.wireOp",EDGE,"E23.3.0.2"),sQuery(id+"F0.wireOp",EDGE,"E23.3.0.3"),sQuery(id+"F0.wireOp",EDGE,"E23.4.0.0"),sQuery(id+"F0.wireOp",EDGE,"E23.4.0.1"),sQuery(id+"F0.wireOp",EDGE,"E23.4.0.2"),sQuery(id+"F0.wireOp",EDGE,"E23.4.0.3"),sQuery(id+"F0.wireOp",EDGE,"E23.5.0.0"),sQuery(id+"F0.wireOp",EDGE,"E23.5.0.1"),sQuery(id+"F0.wireOp",EDGE,"E23.5.0.2"),sQuery(id+"F0.wireOp",EDGE,"E23.5.0.3"),sQuery(id+"F0.wireOp",EDGE,"E23.6.0.0"),sQuery(id+"F0.wireOp",EDGE,"E23.6.0.1"),sQuery(id+"F0.wireOp",EDGE,"E23.6.0.2"),sQuery(id+"F0.wireOp",EDGE,"E23.6.0.3"),sQuery(id+"F0.wireOp",EDGE,"E23.7.0.0"),sQuery(id+"F0.wireOp",EDGE,"E23.7.0.1"),sQuery(id+"F0.wireOp",EDGE,"E23.7.0.2"),sQuery(id+"F0.wireOp",EDGE,"E23.7.0.3"),sQuery(id+"F0.wireOp",EDGE,"E23.8.0.0"),sQuery(id+"F0.wireOp",EDGE,"E23.8.0.1"),sQuery(id+"F0.wireOp",EDGE,"E23.8.0.2"),sQuery(id+"F0.wireOp",EDGE,"E23.8.0.3"),sQuery(id+"F0.wireOp",EDGE,"E23.9.0.0"),sQuery(id+"F0.wireOp",EDGE,"E23.9.0.1"),sQuery(id+"F0.wireOp",EDGE,"E23.9.0.2"),sQuery(id+"F0.wireOp",EDGE,"E23.9.0.3"),sQuery(id+"F0.wireOp",EDGE,"E23.10.0.0"),sQuery(id+"F0.wireOp",EDGE,"E23.10.0.1"),sQuery(id+"F0.wireOp",EDGE,"E23.10.0.2"),sQuery(id+"F0.wireOp",EDGE,"E23.10.0.3"),sQuery(id+"F0.wireOp",EDGE,"E23.11.0.0"),sQuery(id+"F0.wireOp",EDGE,"E23.11.0.1"),sQuery(id+"F0.wireOp",EDGE,"E23.11.0.2"),sQuery(id+"F0.wireOp",EDGE,"E23.11.0.3"),sQuery(id+"F0.wireOp",EDGE,"E23.12.0.0"),sQuery(id+"F0.wireOp",EDGE,"E23.12.0.1"),sQuery(id+"F0.wireOp",EDGE,"E23.12.0.2"),sQuery(id+"F0.wireOp",EDGE,"E23.12.0.3"),sQuery(id+"F0.wireOp",EDGE,"E23.13.0.0"),sQuery(id+"F0.wireOp",EDGE,"E23.13.0.1"),sQuery(id+"F0.wireOp",EDGE,"E23.13.0.2"),sQuery(id+"F0.wireOp",EDGE,"E23.13.0.3"),sQuery(id+"F0.wireOp",EDGE,"E25.1.0.0"),sQuery(id+"F0.wireOp",EDGE,"E25.1.0.1"),sQuery(id+"F0.wireOp",EDGE,"E25.1.0.2"),sQuery(id+"F0.wireOp",EDGE,"E25.1.0.3"),sQuery(id+"F0.wireOp",EDGE,"E25.1.0.4"),sQuery(id+"F0.wireOp",EDGE,"E25.1.0.5"),sQuery(id+"F0.wireOp",EDGE,"E25.1.0.6"),sQuery(id+"F0.wireOp",EDGE,"E25.1.0.7"),sQuery(id+"F0.wireOp",EDGE,"E25.1.0.8"),sQuery(id+"F0.wireOp",EDGE,"E25.1.0.9"),sQuery(id+"F0.wireOp",EDGE,"E25.1.0.10"),sQuery(id+"F0.wireOp",EDGE,"E25.1.0.11"),sQuery(id+"F0.wireOp",EDGE,"E25.2.0.0"),sQuery(id+"F0.wireOp",EDGE,"E25.2.0.1"),sQuery(id+"F0.wireOp",EDGE,"E25.2.0.2"),sQuery(id+"F0.wireOp",EDGE,"E25.2.0.3"),sQuery(id+"F0.wireOp",EDGE,"E25.2.0.4"),sQuery(id+"F0.wireOp",EDGE,"E25.2.0.5"),sQuery(id+"F0.wireOp",EDGE,"E25.2.0.6"),sQuery(id+"F0.wireOp",EDGE,"E25.2.0.7"),sQuery(id+"F0.wireOp",EDGE,"E25.2.0.8"),sQuery(id+"F0.wireOp",EDGE,"E25.2.0.9"),sQuery(id+"F0.wireOp",EDGE,"E25.2.0.10"),sQuery(id+"F0.wireOp",EDGE,"E25.2.0.11"),sQuery(id+"F0.wireOp",EDGE,"E26.1.0.0"),sQuery(id+"F0.wireOp",EDGE,"E26.1.0.1"),sQuery(id+"F0.wireOp",EDGE,"E26.1.0.2"),sQuery(id+"F0.wireOp",EDGE,"E26.1.0.3"),sQuery(id+"F0.wireOp",EDGE,"E26.1.0.4"),sQuery(id+"F0.wireOp",EDGE,"E26.1.0.5"),sQuery(id+"F0.wireOp",EDGE,"E26.1.0.6"),sQuery(id+"F0.wireOp",EDGE,"E26.1.0.7"),sQuery(id+"F0.wireOp",EDGE,"E26.1.0.8"),sQuery(id+"F0.wireOp",EDGE,"E26.1.0.9"),sQuery(id+"F0.wireOp",EDGE,"E26.1.0.10"),sQuery(id+"F0.wireOp",EDGE,"E26.1.0.11"),sQuery(id+"F0.wireOp",EDGE,"E28.bottom"),sQuery(id+"F0.wireOp",EDGE,"E28.top"),sQuery(id+"F0.wireOp",EDGE,"E28.left"),sQuery(id+"F0.wireOp",EDGE,"E28.right")])]});
            transform(context, id + "F6", {"entities" : qUnion([Q0]), "transformType" : TransformType.TRANSLATION_3D, "dx" : 0 * mm, "dy" : 127 * mm, "dz" : 0 * mm, "makeCopy" : true});
        }
        {
            var Q0;
            Q0=makeQuery(id+"F6.opPattern","COPY",BODY,{"derivedFrom":makeQuery(id+"F1.opExtrude","SWEPT_BODY",BODY,{"disambiguationData":[OSD([sQuery(id+"F0.wireOp",EDGE,"E20.bottom"),sQuery(id+"F0.wireOp",EDGE,"E20.top"),sQuery(id+"F0.wireOp",EDGE,"E20.left"),sQuery(id+"F0.wireOp",EDGE,"E20.right"),sQuery(id+"F0.wireOp",EDGE,"E21.0.1.0"),sQuery(id+"F0.wireOp",EDGE,"E21.0.1.1"),sQuery(id+"F0.wireOp",EDGE,"E21.0.1.2"),sQuery(id+"F0.wireOp",EDGE,"E21.0.1.3"),sQuery(id+"F0.wireOp",EDGE,"E21.1.0.0"),sQuery(id+"F0.wireOp",EDGE,"E21.1.0.1"),sQuery(id+"F0.wireOp",EDGE,"E21.1.0.2"),sQuery(id+"F0.wireOp",EDGE,"E21.1.0.3"),sQuery(id+"F0.wireOp",EDGE,"E21.1.1.0"),sQuery(id+"F0.wireOp",EDGE,"E21.1.1.1"),sQuery(id+"F0.wireOp",EDGE,"E21.1.1.2"),sQuery(id+"F0.wireOp",EDGE,"E21.1.1.3"),sQuery(id+"F0.wireOp",EDGE,"E21.2.0.0"),sQuery(id+"F0.wireOp",EDGE,"E21.2.0.1"),sQuery(id+"F0.wireOp",EDGE,"E21.2.0.2"),sQuery(id+"F0.wireOp",EDGE,"E21.2.0.3"),sQuery(id+"F0.wireOp",EDGE,"E21.2.1.0"),sQuery(id+"F0.wireOp",EDGE,"E21.2.1.1"),sQuery(id+"F0.wireOp",EDGE,"E21.2.1.2"),sQuery(id+"F0.wireOp",EDGE,"E21.2.1.3"),sQuery(id+"F0.wireOp",EDGE,"E21.3.0.0"),sQuery(id+"F0.wireOp",EDGE,"E21.3.0.1"),sQuery(id+"F0.wireOp",EDGE,"E21.3.0.2"),sQuery(id+"F0.wireOp",EDGE,"E21.3.0.3"),sQuery(id+"F0.wireOp",EDGE,"E21.3.1.0"),sQuery(id+"F0.wireOp",EDGE,"E21.3.1.1"),sQuery(id+"F0.wireOp",EDGE,"E21.3.1.2"),sQuery(id+"F0.wireOp",EDGE,"E21.3.1.3"),sQuery(id+"F0.wireOp",EDGE,"E21.4.0.0"),sQuery(id+"F0.wireOp",EDGE,"E21.4.0.1"),sQuery(id+"F0.wireOp",EDGE,"E21.4.0.2"),sQuery(id+"F0.wireOp",EDGE,"E21.4.0.3"),sQuery(id+"F0.wireOp",EDGE,"E21.4.1.0"),sQuery(id+"F0.wireOp",EDGE,"E21.4.1.1"),sQuery(id+"F0.wireOp",EDGE,"E21.4.1.2"),sQuery(id+"F0.wireOp",EDGE,"E21.4.1.3"),sQuery(id+"F0.wireOp",EDGE,"E21.5.0.0"),sQuery(id+"F0.wireOp",EDGE,"E21.5.0.1"),sQuery(id+"F0.wireOp",EDGE,"E21.5.0.2"),sQuery(id+"F0.wireOp",EDGE,"E21.5.0.3"),sQuery(id+"F0.wireOp",EDGE,"E21.5.1.0"),sQuery(id+"F0.wireOp",EDGE,"E21.5.1.1"),sQuery(id+"F0.wireOp",EDGE,"E21.5.1.2"),sQuery(id+"F0.wireOp",EDGE,"E21.5.1.3"),sQuery(id+"F0.wireOp",EDGE,"E21.6.0.0"),sQuery(id+"F0.wireOp",EDGE,"E21.6.0.1"),sQuery(id+"F0.wireOp",EDGE,"E21.6.0.2"),sQuery(id+"F0.wireOp",EDGE,"E21.6.0.3"),sQuery(id+"F0.wireOp",EDGE,"E21.6.1.0"),sQuery(id+"F0.wireOp",EDGE,"E21.6.1.1"),sQuery(id+"F0.wireOp",EDGE,"E21.6.1.2"),sQuery(id+"F0.wireOp",EDGE,"E21.6.1.3"),sQuery(id+"F0.wireOp",EDGE,"E21.7.0.0"),sQuery(id+"F0.wireOp",EDGE,"E21.7.0.1"),sQuery(id+"F0.wireOp",EDGE,"E21.7.0.2"),sQuery(id+"F0.wireOp",EDGE,"E21.7.0.3"),sQuery(id+"F0.wireOp",EDGE,"E21.7.1.0"),sQuery(id+"F0.wireOp",EDGE,"E21.7.1.1"),sQuery(id+"F0.wireOp",EDGE,"E21.7.1.2"),sQuery(id+"F0.wireOp",EDGE,"E21.7.1.3"),sQuery(id+"F0.wireOp",EDGE,"E21.8.0.0"),sQuery(id+"F0.wireOp",EDGE,"E21.8.0.1"),sQuery(id+"F0.wireOp",EDGE,"E21.8.0.2"),sQuery(id+"F0.wireOp",EDGE,"E21.8.0.3"),sQuery(id+"F0.wireOp",EDGE,"E21.8.1.0"),sQuery(id+"F0.wireOp",EDGE,"E21.8.1.1"),sQuery(id+"F0.wireOp",EDGE,"E21.8.1.2"),sQuery(id+"F0.wireOp",EDGE,"E21.8.1.3"),sQuery(id+"F0.wireOp",EDGE,"E21.9.0.0"),sQuery(id+"F0.wireOp",EDGE,"E21.9.0.1"),sQuery(id+"F0.wireOp",EDGE,"E21.9.0.2"),sQuery(id+"F0.wireOp",EDGE,"E21.9.0.3"),sQuery(id+"F0.wireOp",EDGE,"E21.9.1.0"),sQuery(id+"F0.wireOp",EDGE,"E21.9.1.1"),sQuery(id+"F0.wireOp",EDGE,"E21.9.1.2"),sQuery(id+"F0.wireOp",EDGE,"E21.9.1.3"),sQuery(id+"F0.wireOp",EDGE,"E21.10.0.0"),sQuery(id+"F0.wireOp",EDGE,"E21.10.0.1"),sQuery(id+"F0.wireOp",EDGE,"E21.10.0.2"),sQuery(id+"F0.wireOp",EDGE,"E21.10.0.3"),sQuery(id+"F0.wireOp",EDGE,"E21.10.1.0"),sQuery(id+"F0.wireOp",EDGE,"E21.10.1.1"),sQuery(id+"F0.wireOp",EDGE,"E21.10.1.2"),sQuery(id+"F0.wireOp",EDGE,"E21.10.1.3"),sQuery(id+"F0.wireOp",EDGE,"E21.11.0.0"),sQuery(id+"F0.wireOp",EDGE,"E21.11.0.1"),sQuery(id+"F0.wireOp",EDGE,"E21.11.0.2"),sQuery(id+"F0.wireOp",EDGE,"E21.11.0.3"),sQuery(id+"F0.wireOp",EDGE,"E21.11.1.0"),sQuery(id+"F0.wireOp",EDGE,"E21.11.1.1"),sQuery(id+"F0.wireOp",EDGE,"E21.11.1.2"),sQuery(id+"F0.wireOp",EDGE,"E21.11.1.3"),sQuery(id+"F0.wireOp",EDGE,"E21.12.0.0"),sQuery(id+"F0.wireOp",EDGE,"E21.12.0.1"),sQuery(id+"F0.wireOp",EDGE,"E21.12.0.2"),sQuery(id+"F0.wireOp",EDGE,"E21.12.0.3"),sQuery(id+"F0.wireOp",EDGE,"E21.12.1.0"),sQuery(id+"F0.wireOp",EDGE,"E21.12.1.1"),sQuery(id+"F0.wireOp",EDGE,"E21.12.1.2"),sQuery(id+"F0.wireOp",EDGE,"E21.12.1.3"),sQuery(id+"F0.wireOp",EDGE,"E21.13.0.0"),sQuery(id+"F0.wireOp",EDGE,"E21.13.0.1"),sQuery(id+"F0.wireOp",EDGE,"E21.13.0.2"),sQuery(id+"F0.wireOp",EDGE,"E21.13.0.3"),sQuery(id+"F0.wireOp",EDGE,"E21.13.1.0"),sQuery(id+"F0.wireOp",EDGE,"E21.13.1.1"),sQuery(id+"F0.wireOp",EDGE,"E21.13.1.2"),sQuery(id+"F0.wireOp",EDGE,"E21.13.1.3"),sQuery(id+"F0.wireOp",EDGE,"E21.14.0.0"),sQuery(id+"F0.wireOp",EDGE,"E21.14.0.1"),sQuery(id+"F0.wireOp",EDGE,"E21.14.0.2"),sQuery(id+"F0.wireOp",EDGE,"E21.14.0.3"),sQuery(id+"F0.wireOp",EDGE,"E21.14.1.0"),sQuery(id+"F0.wireOp",EDGE,"E21.14.1.1"),sQuery(id+"F0.wireOp",EDGE,"E21.14.1.2"),sQuery(id+"F0.wireOp",EDGE,"E21.14.1.3"),sQuery(id+"F0.wireOp",EDGE,"E22.bottom"),sQuery(id+"F0.wireOp",EDGE,"E22.top"),sQuery(id+"F0.wireOp",EDGE,"E22.left"),sQuery(id+"F0.wireOp",EDGE,"E22.right"),sQuery(id+"F0.wireOp",EDGE,"E23.1.0.0"),sQuery(id+"F0.wireOp",EDGE,"E23.1.0.1"),sQuery(id+"F0.wireOp",EDGE,"E23.1.0.2"),sQuery(id+"F0.wireOp",EDGE,"E23.1.0.3"),sQuery(id+"F0.wireOp",EDGE,"E23.2.0.0"),sQuery(id+"F0.wireOp",EDGE,"E23.2.0.1"),sQuery(id+"F0.wireOp",EDGE,"E23.2.0.2"),sQuery(id+"F0.wireOp",EDGE,"E23.2.0.3"),sQuery(id+"F0.wireOp",EDGE,"E23.3.0.0"),sQuery(id+"F0.wireOp",EDGE,"E23.3.0.1"),sQuery(id+"F0.wireOp",EDGE,"E23.3.0.2"),sQuery(id+"F0.wireOp",EDGE,"E23.3.0.3"),sQuery(id+"F0.wireOp",EDGE,"E23.4.0.0"),sQuery(id+"F0.wireOp",EDGE,"E23.4.0.1"),sQuery(id+"F0.wireOp",EDGE,"E23.4.0.2"),sQuery(id+"F0.wireOp",EDGE,"E23.4.0.3"),sQuery(id+"F0.wireOp",EDGE,"E23.5.0.0"),sQuery(id+"F0.wireOp",EDGE,"E23.5.0.1"),sQuery(id+"F0.wireOp",EDGE,"E23.5.0.2"),sQuery(id+"F0.wireOp",EDGE,"E23.5.0.3"),sQuery(id+"F0.wireOp",EDGE,"E23.6.0.0"),sQuery(id+"F0.wireOp",EDGE,"E23.6.0.1"),sQuery(id+"F0.wireOp",EDGE,"E23.6.0.2"),sQuery(id+"F0.wireOp",EDGE,"E23.6.0.3"),sQuery(id+"F0.wireOp",EDGE,"E23.7.0.0"),sQuery(id+"F0.wireOp",EDGE,"E23.7.0.1"),sQuery(id+"F0.wireOp",EDGE,"E23.7.0.2"),sQuery(id+"F0.wireOp",EDGE,"E23.7.0.3"),sQuery(id+"F0.wireOp",EDGE,"E23.8.0.0"),sQuery(id+"F0.wireOp",EDGE,"E23.8.0.1"),sQuery(id+"F0.wireOp",EDGE,"E23.8.0.2"),sQuery(id+"F0.wireOp",EDGE,"E23.8.0.3"),sQuery(id+"F0.wireOp",EDGE,"E23.9.0.0"),sQuery(id+"F0.wireOp",EDGE,"E23.9.0.1"),sQuery(id+"F0.wireOp",EDGE,"E23.9.0.2"),sQuery(id+"F0.wireOp",EDGE,"E23.9.0.3"),sQuery(id+"F0.wireOp",EDGE,"E23.10.0.0"),sQuery(id+"F0.wireOp",EDGE,"E23.10.0.1"),sQuery(id+"F0.wireOp",EDGE,"E23.10.0.2"),sQuery(id+"F0.wireOp",EDGE,"E23.10.0.3"),sQuery(id+"F0.wireOp",EDGE,"E23.11.0.0"),sQuery(id+"F0.wireOp",EDGE,"E23.11.0.1"),sQuery(id+"F0.wireOp",EDGE,"E23.11.0.2"),sQuery(id+"F0.wireOp",EDGE,"E23.11.0.3"),sQuery(id+"F0.wireOp",EDGE,"E23.12.0.0"),sQuery(id+"F0.wireOp",EDGE,"E23.12.0.1"),sQuery(id+"F0.wireOp",EDGE,"E23.12.0.2"),sQuery(id+"F0.wireOp",EDGE,"E23.12.0.3"),sQuery(id+"F0.wireOp",EDGE,"E23.13.0.0"),sQuery(id+"F0.wireOp",EDGE,"E23.13.0.1"),sQuery(id+"F0.wireOp",EDGE,"E23.13.0.2"),sQuery(id+"F0.wireOp",EDGE,"E23.13.0.3"),sQuery(id+"F0.wireOp",EDGE,"E25.1.0.0"),sQuery(id+"F0.wireOp",EDGE,"E25.1.0.1"),sQuery(id+"F0.wireOp",EDGE,"E25.1.0.2"),sQuery(id+"F0.wireOp",EDGE,"E25.1.0.3"),sQuery(id+"F0.wireOp",EDGE,"E25.1.0.4"),sQuery(id+"F0.wireOp",EDGE,"E25.1.0.5"),sQuery(id+"F0.wireOp",EDGE,"E25.1.0.6"),sQuery(id+"F0.wireOp",EDGE,"E25.1.0.7"),sQuery(id+"F0.wireOp",EDGE,"E25.1.0.8"),sQuery(id+"F0.wireOp",EDGE,"E25.1.0.9"),sQuery(id+"F0.wireOp",EDGE,"E25.1.0.10"),sQuery(id+"F0.wireOp",EDGE,"E25.1.0.11"),sQuery(id+"F0.wireOp",EDGE,"E25.2.0.0"),sQuery(id+"F0.wireOp",EDGE,"E25.2.0.1"),sQuery(id+"F0.wireOp",EDGE,"E25.2.0.2"),sQuery(id+"F0.wireOp",EDGE,"E25.2.0.3"),sQuery(id+"F0.wireOp",EDGE,"E25.2.0.4"),sQuery(id+"F0.wireOp",EDGE,"E25.2.0.5"),sQuery(id+"F0.wireOp",EDGE,"E25.2.0.6"),sQuery(id+"F0.wireOp",EDGE,"E25.2.0.7"),sQuery(id+"F0.wireOp",EDGE,"E25.2.0.8"),sQuery(id+"F0.wireOp",EDGE,"E25.2.0.9"),sQuery(id+"F0.wireOp",EDGE,"E25.2.0.10"),sQuery(id+"F0.wireOp",EDGE,"E25.2.0.11"),sQuery(id+"F0.wireOp",EDGE,"E26.1.0.0"),sQuery(id+"F0.wireOp",EDGE,"E26.1.0.1"),sQuery(id+"F0.wireOp",EDGE,"E26.1.0.2"),sQuery(id+"F0.wireOp",EDGE,"E26.1.0.3"),sQuery(id+"F0.wireOp",EDGE,"E26.1.0.4"),sQuery(id+"F0.wireOp",EDGE,"E26.1.0.5"),sQuery(id+"F0.wireOp",EDGE,"E26.1.0.6"),sQuery(id+"F0.wireOp",EDGE,"E26.1.0.7"),sQuery(id+"F0.wireOp",EDGE,"E26.1.0.8"),sQuery(id+"F0.wireOp",EDGE,"E26.1.0.9"),sQuery(id+"F0.wireOp",EDGE,"E26.1.0.10"),sQuery(id+"F0.wireOp",EDGE,"E26.1.0.11"),sQuery(id+"F0.wireOp",EDGE,"E28.bottom"),sQuery(id+"F0.wireOp",EDGE,"E28.top"),sQuery(id+"F0.wireOp",EDGE,"E28.left"),sQuery(id+"F0.wireOp",EDGE,"E28.right")])]}),"instanceName":"1"});
            var Q1;
            Q1=makeQuery(id+"F6.opPattern","COPY",EDGE,{"derivedFrom":makeQuery(id+"F1.opExtrude","CAP_EDGE",EDGE,{"disambiguationData":[OSD([sQuery(id+"F0.wireOp",EDGE,"E28.right")])],"isStart":false}),"instanceName":"1"});
            transform(context, id + "F7", {"entities" : qUnion([Q0]), "transformType" : TransformType.ROTATION, "transformAxis" : qUnion([Q1]), "angle" : 180 * degree, "makeCopy" : false});
        }
        {
            var Q0;
            Q0=makeQuery(id+"F5.boolean.opBoolean","MERGE",FACE,{"derivedFrom":[makeQuery(id+"F3.boolean.opBoolean","MERGE",FACE,{"derivedFrom":[makeQuery(id+"F1.opExtrude","SWEPT_FACE",FACE,{"disambiguationData":[OSD([sQuery(id+"F0.wireOp",EDGE,"E28.top")])]}),makeQuery(id+"F3.opExtrude","SWEPT_FACE",FACE,{"disambiguationData":[OSD([sQuery(id+"F2.wireOp",EDGE,"E36")])]})]}),makeQuery(id+"F5.opExtrude","SWEPT_FACE",FACE,{"disambiguationData":[OSD([sQuery(id+"F4.wireOp",EDGE,"E40")])]})]});
            var sketch = newSketch(context, id + "F8", { "sketchPlane" : qUnion([Q0])});
            skLineSegment(sketch, "E43.bottom", {"start": v(-80.06, 6.35) * mm, "end": v(-69.9, 6.35) * mm});
            skLineSegment(sketch, "E43.top", {"start": v(-80.06, 0) * mm, "end": v(-69.9, 0) * mm});
            skLineSegment(sketch, "E43.left", {"start": v(-80.06, 6.35) * mm, "end": v(-80.06, 0) * mm});
            skLineSegment(sketch, "E43.right", {"start": v(-69.9, 6.35) * mm, "end": v(-69.9, 0) * mm});
            skLineSegment(sketch, "E44.bottom", {"start": v(-103.05, -31.75) * mm, "end": v(-99.24, -31.75) * mm});
            skLineSegment(sketch, "E44.top", {"start": v(-103.05, -25.4) * mm, "end": v(-99.24, -25.4) * mm});
            skLineSegment(sketch, "E44.left", {"start": v(-103.05, -31.75) * mm, "end": v(-103.05, -25.4) * mm});
            skLineSegment(sketch, "E44.right", {"start": v(-99.24, -31.75) * mm, "end": v(-99.24, -25.4) * mm});
            skLineSegment(sketch, "E45", {"start": v(11.25, 0) * mm, "end": v(6.17, 0) * mm});
            skLineSegment(sketch, "E46", {"start": v(6.17, 0) * mm, "end": v(6.17, 6.35) * mm});
            skLineSegment(sketch, "E47", {"start": v(6.17, 6.35) * mm, "end": v(11.25, 6.35) * mm});
            skLineSegment(sketch, "E48.MirrorCS", {"start": v(16.33, 6.35) * mm, "end": v(11.25, 6.35) * mm});
            skLineSegment(sketch, "E49.MirrorCS", {"start": v(16.33, 0) * mm, "end": v(16.33, 6.35) * mm});
            skLineSegment(sketch, "E50.MirrorCS", {"start": v(11.25, 0) * mm, "end": v(16.33, 0) * mm});
            skLineSegment(sketch, "E51.MirrorCS", {"start": v(102.55, 6.35) * mm, "end": v(92.4, 6.35) * mm});
            skLineSegment(sketch, "E52.MirrorCS", {"start": v(92.4, 6.35) * mm, "end": v(92.4, 0) * mm});
            skLineSegment(sketch, "E53.MirrorCS", {"start": v(102.55, 0) * mm, "end": v(92.4, 0) * mm});
            skLineSegment(sketch, "E54.MirrorCS", {"start": v(102.55, 6.35) * mm, "end": v(102.55, 0) * mm});
            skLineSegment(sketch, "E55.MirrorCS", {"start": v(121.74, -31.75) * mm, "end": v(121.74, -25.4) * mm});
            skLineSegment(sketch, "E56.MirrorCS", {"start": v(125.55, -25.4) * mm, "end": v(121.74, -25.4) * mm});
            skLineSegment(sketch, "E57.MirrorCS", {"start": v(125.55, -31.75) * mm, "end": v(125.55, -25.4) * mm});
            skLineSegment(sketch, "E58.MirrorCS", {"start": v(125.55, -31.75) * mm, "end": v(121.74, -31.75) * mm});
            skSolve(sketch);
        }
        {
            var Q0;
            Q0 = qSketchRegion(id + "F8", true);
            extrude(context, id + "F9", {"entities" : qUnion([Q0]), "operationType" : NewBodyOperationType.ADD, "depth" : 3.8 * mm});
        }
    });
